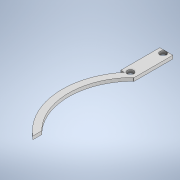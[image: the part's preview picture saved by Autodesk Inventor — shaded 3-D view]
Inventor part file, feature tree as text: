
AUTODESK INVENTOR PART (.ipt)
format: ipt  version: 2021 (Build 250183000, 183)  size: 125,952 bytes
history: native  units: in
note: dims shown in document units (in); Inventor stores cm internally (conversion verified against a paired STEP export)
features: sketch x2, extrude x1, hole x1, projected_geometry x1
ambient origin geometry x8: Origin, YZ Plane, XZ Plane, XY Plane, X Axis, Y Axis, Z Axis, Center Point
bodies: Solid1 (feature_tree)
feature tree (5):
  extrude  "Extrusion1"  Depth=0.5in
  hole  "Hole1"  [1 undecoded]
  sketch  "Sketch1"  dims[d0=2.5in d2=0.5in]
  sketch  "Sketch2"  dims[d3=1.5in d4=0.125in d5=0.0in d6=0.5in d7=0.25in d8=0.25in d9=1.25in d10=1.5in d11=0.125in d12=0.25in d13=0.75in d14=0.375in d15=0.25in d16=0.5635in d17=0.75in d18=0.8108in]
  projected_geometry  "Projected Loop1"
note: 1 required parameter value undecoded (feature->parameter linkage not recoverable at this tier; creation-order binding heuristic only, values carry confidence <= 0.55)
